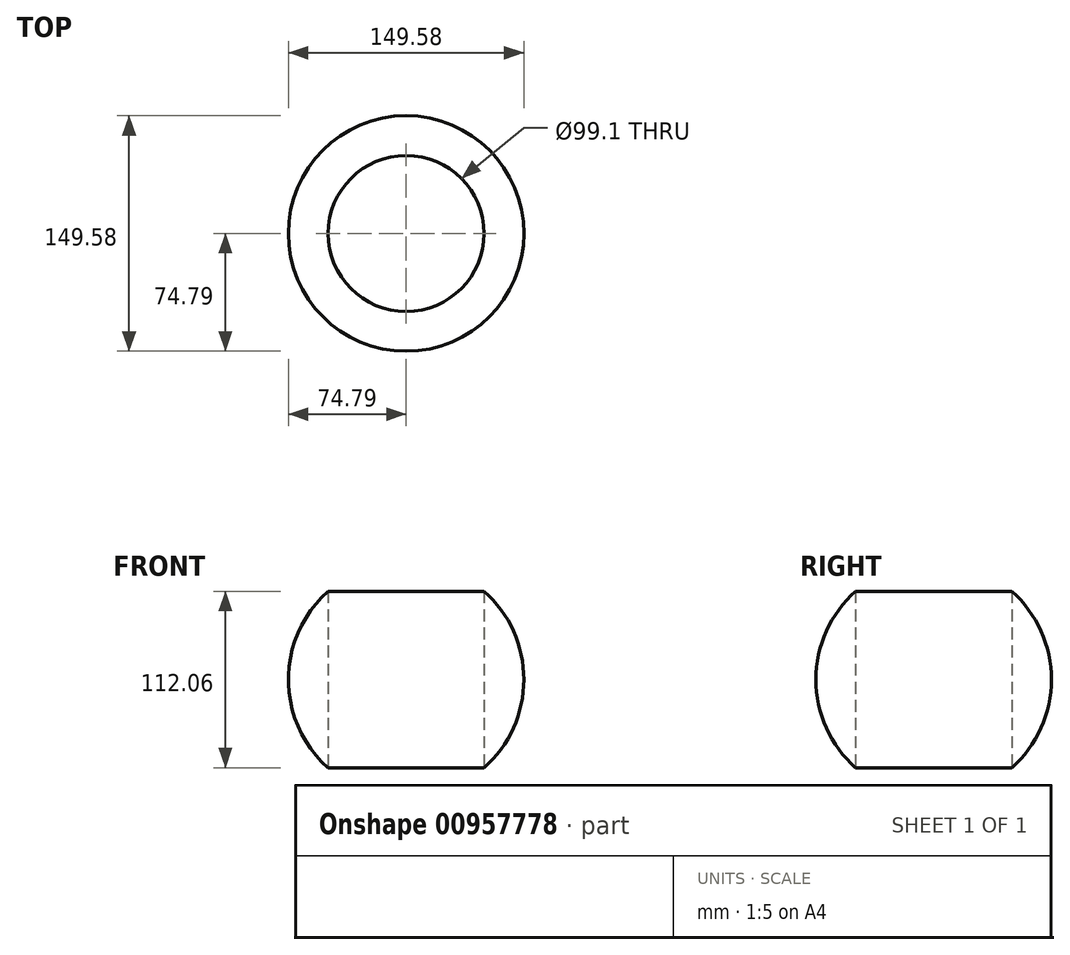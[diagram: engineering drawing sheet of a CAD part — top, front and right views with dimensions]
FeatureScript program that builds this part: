
annotation { "Feature Type Name" : "Feature", "Feature Type Description" : "" }
export const myFeature = defineFeature(function(context is Context, id is Id, definition is map)
    precondition{}
    {
        {
            var Q0;
            Q0=qCreatedBy(makeId("Front.planeOp"),FACE);
            var sketch = newSketch(context, id + "F0", { "sketchPlane" : qUnion([Q0])});
            skArc(sketch, "E0", {"start": v(0, 74.8) * mm, "mid": v(-74.8, 0) * mm, "end": v(0, -74.8) * mm});
            skLineSegment(sketch, "E1", {"start": v(0, 0) * mm, "end": v(0, 172.2) * mm, "construction": true});
            skLineSegment(sketch, "E2", {"start": v(0, 74.8) * mm, "end": v(0, -74.8) * mm});
            skSolve(sketch);
        }
        {
            var Q0;
            Q0=makeQuery(id+"F0.imprint","IMPRINT",FACE,{"disambiguationData":[TD([[makeQuery(id+"F0.imprint","IMPRINT",EDGE,{"derivedFrom":sQuery(id+"F0.wireOp",EDGE,"E0")}),1.0]])]});
            var Q1;
            Q1=sQuery(id+"F0.wireOp",EDGE,"E1");
            revolve(context, id + "F1", {"surfaceOperationType" : NewSurfaceOperationType.NEW, "entities" : qUnion([Q0]), "axis" : qUnion([Q1]), "revolveType" : RevolveType.FULL});
        }
        {
            var Q0;
            Q0=qCreatedBy(makeId("Top.planeOp"),FACE);
            var sketch = newSketch(context, id + "F2", { "sketchPlane" : qUnion([Q0])});
            skCircle(sketch, "E3", {"center": v(0, 0) * mm, "radius": 49.55 * mm});
            skSolve(sketch);
        }
        {
            var Q0;
            Q0 = qSketchRegion(id + "F2", true);
            extrude(context, id + "F3", {"entities" : qUnion([Q0]), "operationType" : NewBodyOperationType.REMOVE, "endBound" : BoundingType.THROUGH_ALL, "depth" : 25 * mm, "offsetDistance" : 25 * mm, "hasSecondDirection" : true, "secondDirectionBound" : SecondDirectionBoundingType.THROUGH_ALL, "secondDirectionOppositeDirection" : true, "secondDirectionDepth" : 25 * mm});
        }
    });
